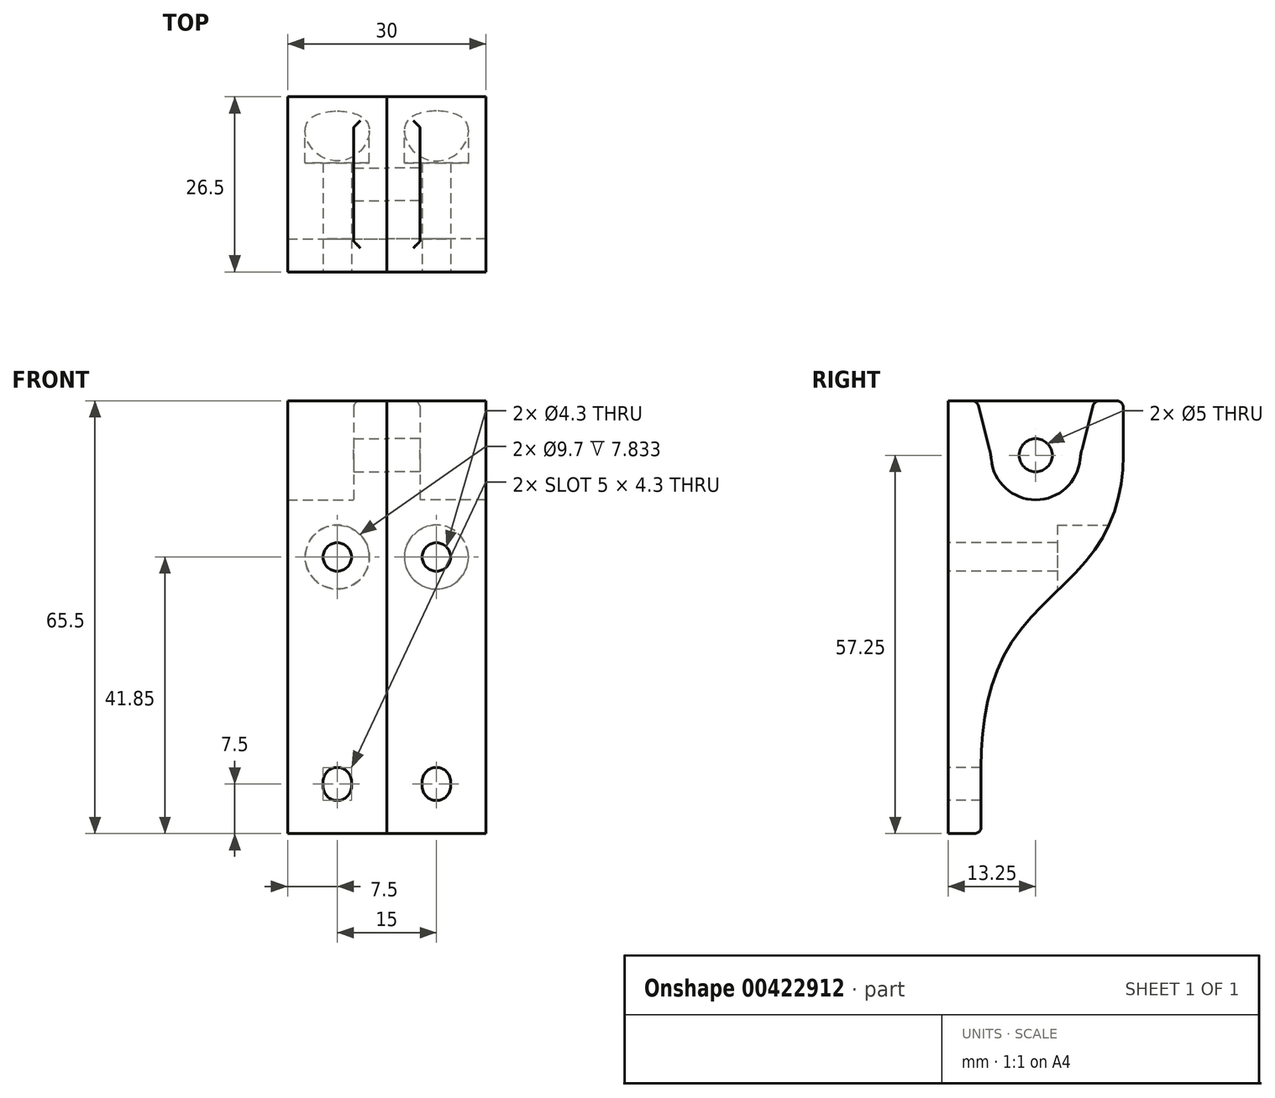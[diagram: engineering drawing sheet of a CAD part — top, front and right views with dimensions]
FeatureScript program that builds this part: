
annotation { "Feature Type Name" : "Feature", "Feature Type Description" : "" }
export const myFeature = defineFeature(function(context is Context, id is Id, definition is map)
    precondition{}
    {
        {
            var Q0;
            Q0=qCreatedBy(makeId("Right.planeOp"),FACE);
            var sketch = newSketch(context, id + "F0", { "sketchPlane" : qUnion([Q0])});
            skArc(sketch, "E0", {"start": v(-6.75, 0) * mm, "mid": v(0, -6.75) * mm, "end": v(6.75, 0) * mm});
            skLineSegment(sketch, "E1", {"start": v(-13.25, 8.25) * mm, "end": v(-13.25, -57.25) * mm});
            skLineSegment(sketch, "E2", {"start": v(10.34, -12.05) * mm, "end": v(-13.25, -12.05) * mm, "construction": true});
            skLineSegment(sketch, "E3.0", {"start": v(7.31, -16.35) * mm, "end": v(-13.25, -16.35) * mm, "construction": true});
            skLineSegment(sketch, "E4.0", {"start": v(-8.25, -47.25) * mm, "end": v(-13.25, -47.25) * mm, "construction": true});
            skLineSegment(sketch, "E5.0", {"start": v(-8.25, -52.25) * mm, "end": v(-13.25, -52.25) * mm, "construction": true});
            skLineSegment(sketch, "E6", {"start": v(-13.25, -57.25) * mm, "end": v(-8.25, -57.25) * mm});
            skFitSpline(sketch, "E7", {"points": [v(-8.25, -47.25) * mm, v(-3.54, -28.12) * mm, v(8.8, -14.49) * mm, v(13.25, 0) * mm], "startDerivative": vector(0, 59.03) * mm, "endDerivative": vector(0, 50.16) * mm});
            skLineSegment(sketch, "E8", {"start": v(13.25, 8.25) * mm, "end": v(13.25, 0) * mm});
            skLineSegment(sketch, "E9", {"start": v(-8.87, 8.25) * mm, "end": v(-6.75, 0) * mm});
            skLineSegment(sketch, "E10", {"start": v(8.87, 8.25) * mm, "end": v(6.75, 0) * mm});
            skLineSegment(sketch, "E11", {"start": v(-8.87, 8.25) * mm, "end": v(-13.25, 8.25) * mm});
            skLineSegment(sketch, "E12", {"start": v(8.87, 8.25) * mm, "end": v(13.25, 8.25) * mm});
            skLineSegment(sketch, "E13.trimOffspring", {"start": v(-8.25, -47.25) * mm, "end": v(-8.25, -57.25) * mm});
            skSolve(sketch);
        }
        {
            var Q0;
            Q0 = qSketchRegion(id + "F0", true);
            extrude(context, id + "F1", {"entities" : qUnion([Q0]), "depth" : 15 * mm});
        }
        {
            var Q0;
            Q0=makeQuery(id+"F1.opExtrude","SWEPT_FACE",FACE,{"disambiguationData":[OSD([sQuery(id+"F0.wireOp",EDGE,"E1")])]});
            var sketch = newSketch(context, id + "F2", { "sketchPlane" : qUnion([Q0])});
            skArc(sketch, "E14", {"start": v(5.35, -50.1) * mm, "mid": v(7.5, -52.25) * mm, "end": v(9.65, -50.1) * mm});
            skCircle(sketch, "E15", {"center": v(7.5, -15.4) * mm, "radius": 2.15 * mm});
            skArc(sketch, "E16", {"start": v(9.65, -49.4) * mm, "mid": v(7.5, -47.25) * mm, "end": v(5.35, -49.4) * mm});
            skLineSegment(sketch, "E17", {"start": v(5.35, -49.4) * mm, "end": v(5.35, -50.1) * mm});
            skLineSegment(sketch, "E18", {"start": v(7.5, -49.4) * mm, "end": v(7.5, -50.1) * mm, "construction": true});
            skLineSegment(sketch, "E19.MirrorCS", {"start": v(9.65, -49.4) * mm, "end": v(9.65, -50.1) * mm});
            skSolve(sketch);
        }
        {
            var Q0;
            Q0 = qSketchRegion(id + "F2", true);
            extrude(context, id + "F3", {"entities" : qUnion([Q0]), "operationType" : NewBodyOperationType.REMOVE, "endBound" : BoundingType.THROUGH_ALL, "oppositeDirection" : true, "depth" : 25 * mm});
        }
        {
            var Q0;
            Q0=makeQuery(id+"F1.opExtrude","SWEPT_FACE",FACE,{"disambiguationData":[OSD([sQuery(id+"F0.wireOp",EDGE,"E8")])]});
            var sketch = newSketch(context, id + "F4", { "sketchPlane" : qUnion([Q0])});
            skCircle(sketch, "E20.0", {"center": v(-7.5, -15.4) * mm, "radius": 2.15 * mm});
            skCircle(sketch, "E21.0", {"center": v(-7.5, -15.4) * mm, "radius": 4.85 * mm});
            skSolve(sketch);
        }
        {
            var Q0;
            Q0 = qSketchRegion(id + "F4", true);
            extrude(context, id + "F5", {"entities" : qUnion([Q0]), "operationType" : NewBodyOperationType.REMOVE, "oppositeDirection" : true, "depth" : 10 * mm});
        }
        {
            var Q0;
            Q0=makeQuery(id+"F1.opExtrude","SWEPT_EDGE",EDGE,{"disambiguationData":[OSD([sQuery(id+"F0.wireOp",EDGE,"E0"),sQuery(id+"F0.wireOp",EDGE,"E10")])]});
            var Q1;
            Q1=makeQuery(id+"F1.opExtrude","SWEPT_EDGE",EDGE,{"disambiguationData":[OSD([sQuery(id+"F0.wireOp",EDGE,"E0"),sQuery(id+"F0.wireOp",EDGE,"E9")])]});
            fillet(context, id + "F6", {"entities" : qUnion([Q0, Q1]), "radius" : 10 * mm, "tangentPropagation" : true, "allowEdgeOverflow" : false});
        }
        {
            var Q0;
            Q0=makeQuery(id+"F1.opExtrude","SWEPT_EDGE",EDGE,{"disambiguationData":[OSD([sQuery(id+"F0.wireOp",EDGE,"E10"),sQuery(id+"F0.wireOp",EDGE,"E12")])]});
            var Q1;
            Q1=makeQuery(id+"F1.opExtrude","SWEPT_EDGE",EDGE,{"disambiguationData":[OSD([sQuery(id+"F0.wireOp",EDGE,"E8"),sQuery(id+"F0.wireOp",EDGE,"E12")])]});
            var Q2;
            Q2=makeQuery(id+"F1.opExtrude","SWEPT_EDGE",EDGE,{"disambiguationData":[OSD([sQuery(id+"F0.wireOp",EDGE,"E9"),sQuery(id+"F0.wireOp",EDGE,"E11")])]});
            var Q3;
            Q3=makeQuery(id+"F1.opExtrude","SWEPT_EDGE",EDGE,{"disambiguationData":[OSD([sQuery(id+"F0.wireOp",EDGE,"E6"),sQuery(id+"F0.wireOp",EDGE,"E13.trimOffspring")])]});
            fillet(context, id + "F7", {"entities" : qUnion([Q0, Q1, Q2, Q3]), "radius" : 1 * mm, "tangentPropagation" : true, "allowEdgeOverflow" : false});
        }
        {
            var Q0;
            Q0=makeQuery(id+"F1.opExtrude","CAP_FACE",FACE,{"disambiguationData":[OSD([sQuery(id+"F0.wireOp",EDGE,"E0"),sQuery(id+"F0.wireOp",EDGE,"E1"),sQuery(id+"F0.wireOp",EDGE,"E6"),sQuery(id+"F0.wireOp",EDGE,"E7"),sQuery(id+"F0.wireOp",EDGE,"E8"),sQuery(id+"F0.wireOp",EDGE,"E9"),sQuery(id+"F0.wireOp",EDGE,"E10"),sQuery(id+"F0.wireOp",EDGE,"E11"),sQuery(id+"F0.wireOp",EDGE,"E12"),sQuery(id+"F0.wireOp",EDGE,"E13.trimOffspring")])],"isStart":true});
            var sketch = newSketch(context, id + "F8", { "sketchPlane" : qUnion([Q0])});
            skArc(sketch, "E22.0", {"start": v(6.72, -0.62) * mm, "mid": v(0, -6.75) * mm, "end": v(-6.72, -0.62) * mm});
            skArc(sketch, "E23.0", {"start": v(-6.72, -0.62) * mm, "mid": v(-6.83, 0.17) * mm, "end": v(-7, 0.95) * mm});
            skArc(sketch, "E24.0", {"start": v(7, 0.95) * mm, "mid": v(6.83, 0.17) * mm, "end": v(6.72, -0.62) * mm});
            skLineSegment(sketch, "E25.0", {"start": v(8.68, 7.5) * mm, "end": v(7, 0.95) * mm});
            skLineSegment(sketch, "E26.0", {"start": v(-8.68, 7.5) * mm, "end": v(-7, 0.95) * mm});
            skLineSegment(sketch, "E27", {"start": v(-2.5, 0) * mm, "end": v(-6.8, 0) * mm});
            skLineSegment(sketch, "E28", {"start": v(2.5, 0) * mm, "end": v(6.8, 0) * mm});
            skLineSegment(sketch, "E29", {"start": v(-9.64, 8.25) * mm, "end": v(9.64, 8.25) * mm});
            skArc(sketch, "E30.0", {"start": v(-8.68, 7.5) * mm, "mid": v(-9.03, 8.04) * mm, "end": v(-9.64, 8.25) * mm});
            skArc(sketch, "E31.0", {"start": v(9.64, 8.25) * mm, "mid": v(9.03, 8.04) * mm, "end": v(8.68, 7.5) * mm});
            skCircle(sketch, "E32.converted", {"center": v(0, 0) * mm, "radius": 2.5 * mm});
            skSolve(sketch);
        }
        {
            var Q0;
            Q0 = qSketchRegion(id + "F8", true);
            extrude(context, id + "F9", {"entities" : qUnion([Q0]), "operationType" : NewBodyOperationType.ADD, "oppositeDirection" : true, "depth" : 5 * mm});
        }
        {
            var Q0;
            Q0=makeQuery(id+"F9.opExtrude","CAP_EDGE",EDGE,{"disambiguationData":[OSD([sQuery(id+"F8.wireOp",EDGE,"E29")])],"isStart":false});
            fillet(context, id + "F10", {"entities" : qUnion([Q0]), "radius" : 1 * mm, "tangentPropagation" : true, "allowEdgeOverflow" : false});
        }
        {
            var Q0;
            Q0=makeQuery(id+"F1.opExtrude","SWEPT_BODY",BODY,{"disambiguationData":[OSD([sQuery(id+"F0.wireOp",EDGE,"E0"),sQuery(id+"F0.wireOp",EDGE,"E1"),sQuery(id+"F0.wireOp",EDGE,"E6"),sQuery(id+"F0.wireOp",EDGE,"E7"),sQuery(id+"F0.wireOp",EDGE,"E8"),sQuery(id+"F0.wireOp",EDGE,"E9"),sQuery(id+"F0.wireOp",EDGE,"E10"),sQuery(id+"F0.wireOp",EDGE,"E11"),sQuery(id+"F0.wireOp",EDGE,"E12"),sQuery(id+"F0.wireOp",EDGE,"E13.trimOffspring")])]});
            var Q1;
            Q1=makeQuery(id+"F9.boolean.opBoolean","MERGE",FACE,{"derivedFrom":[makeQuery(id+"F1.opExtrude","CAP_FACE",FACE,{"disambiguationData":[OSD([sQuery(id+"F0.wireOp",EDGE,"E0"),sQuery(id+"F0.wireOp",EDGE,"E1"),sQuery(id+"F0.wireOp",EDGE,"E6"),sQuery(id+"F0.wireOp",EDGE,"E7"),sQuery(id+"F0.wireOp",EDGE,"E8"),sQuery(id+"F0.wireOp",EDGE,"E9"),sQuery(id+"F0.wireOp",EDGE,"E10"),sQuery(id+"F0.wireOp",EDGE,"E11"),sQuery(id+"F0.wireOp",EDGE,"E12"),sQuery(id+"F0.wireOp",EDGE,"E13.trimOffspring")])],"isStart":true}),makeQuery(id+"F9.opExtrude","CAP_FACE",FACE,{"disambiguationData":[OSD([sQuery(id+"F8.wireOp",EDGE,"E22.0"),sQuery(id+"F8.wireOp",EDGE,"E23.0"),sQuery(id+"F8.wireOp",EDGE,"E24.0"),sQuery(id+"F8.wireOp",EDGE,"E25.0"),sQuery(id+"F8.wireOp",EDGE,"E26.0"),sQuery(id+"F8.wireOp",EDGE,"E29"),sQuery(id+"F8.wireOp",EDGE,"E30.0"),sQuery(id+"F8.wireOp",EDGE,"E31.0"),sQuery(id+"F8.wireOp",EDGE,"E32.converted")])],"isStart":true})]});
            mirror(context, id + "F11", {"entities" : qUnion([Q0]), "mirrorPlane" : qUnion([Q1])});
        }
    });
